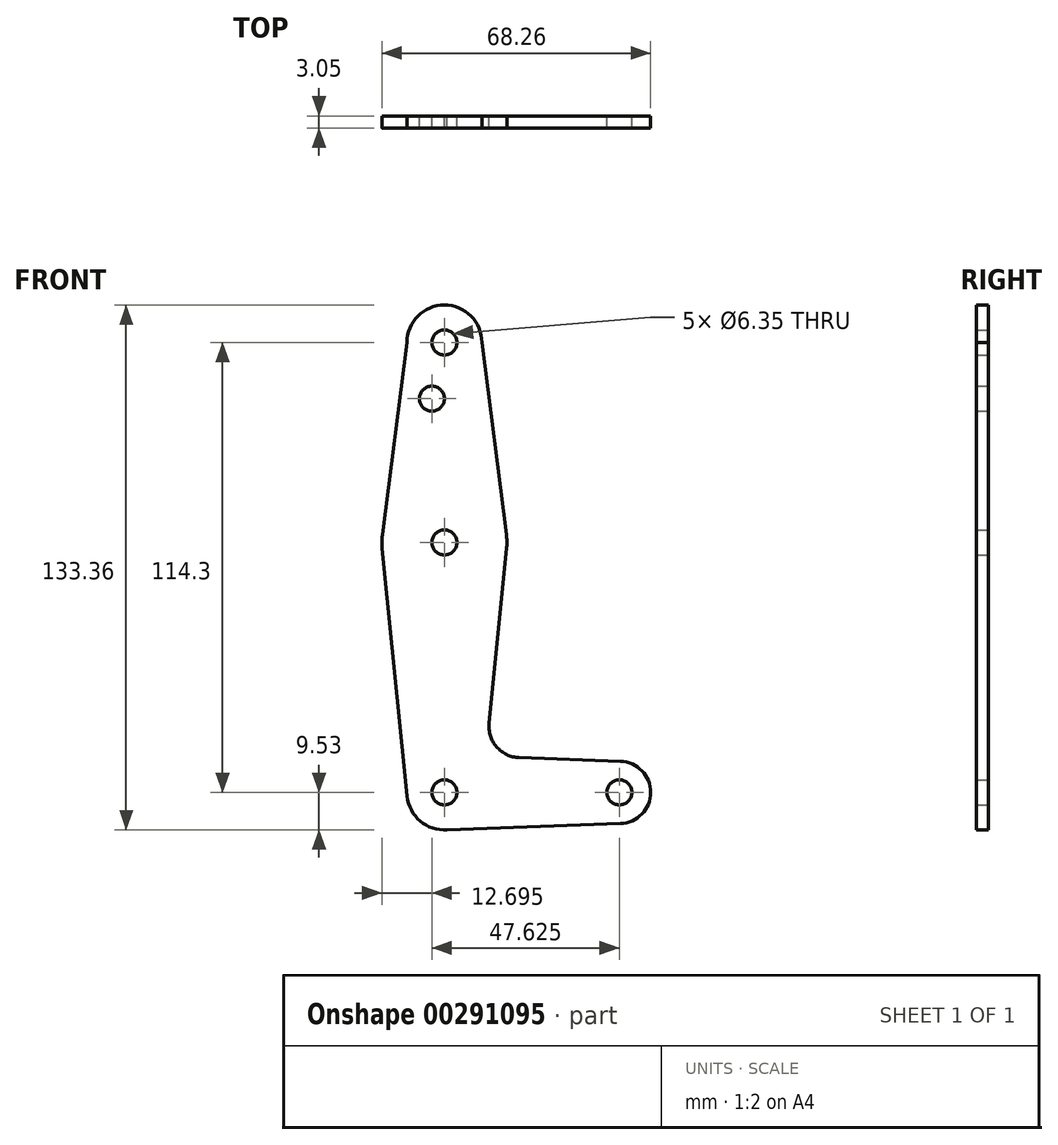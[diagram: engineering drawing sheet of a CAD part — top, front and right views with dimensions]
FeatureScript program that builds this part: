
annotation { "Feature Type Name" : "Feature", "Feature Type Description" : "" }
export const myFeature = defineFeature(function(context is Context, id is Id, definition is map)
    precondition{}
    {
        {
            var Q0;
            Q0=qCreatedBy(makeId("Front.planeOp"),FACE);
            var sketch = newSketch(context, id + "F0", { "sketchPlane" : qUnion([Q0])});
            skLineSegment(sketch, "E0", {"start": v(0, 0) * mm, "end": v(0, 114.3) * mm});
            skLineSegment(sketch, "E1", {"start": v(0, 0) * mm, "end": v(44.45, 0) * mm});
            skCircle(sketch, "E2", {"center": v(0, 114.3) * mm, "radius": 9.53 * mm});
            skCircle(sketch, "E3", {"center": v(0, 63.5) * mm, "radius": 15.88 * mm});
            skCircle(sketch, "E4", {"center": v(0, 0) * mm, "radius": 9.53 * mm});
            skCircle(sketch, "E5", {"center": v(44.45, 0) * mm, "radius": 7.94 * mm});
            skLineSegment(sketch, "E6", {"start": v(-9.53, 114.3) * mm, "end": v(-15.75, 65.5) * mm});
            skLineSegment(sketch, "E7", {"start": v(9.53, 114.3) * mm, "end": v(15.75, 65.5) * mm});
            skLineSegment(sketch, "E8", {"start": v(15.8, 61.91) * mm, "end": v(11.34, 17.59) * mm});
            skLineSegment(sketch, "E9", {"start": v(18.97, 8.85) * mm, "end": v(44.73, 7.93) * mm});
            skLineSegment(sketch, "E10", {"start": v(0, -9.53) * mm, "end": v(44.73, -7.93) * mm});
            skCircle(sketch, "E11", {"center": v(0, 114.3) * mm, "radius": 3.18 * mm});
            skCircle(sketch, "E12", {"center": v(-3.17, 100.03) * mm, "radius": 3.18 * mm});
            skCircle(sketch, "E13", {"center": v(0, 63.5) * mm, "radius": 3.18 * mm});
            skCircle(sketch, "E14", {"center": v(0, 0) * mm, "radius": 3.18 * mm});
            skCircle(sketch, "E15", {"center": v(44.45, 0) * mm, "radius": 3.18 * mm});
            skPoint(sketch, "E16.newPointB", {"position": v(0, 9.53) * mm});
            skArc(sketch, "E16.filletArc", {"start": v(11.34, 17.59) * mm, "mid": v(13.26, 11.57) * mm, "end": v(18.97, 8.85) * mm});
            skLineSegment(sketch, "E17", {"start": v(-15.8, 61.91) * mm, "end": v(-9.48, -0.95) * mm});
            skSolve(sketch);
        }
        {
            var Q0;
            Q0 = qSketchRegion(id + "F0", true);
            var Q1;
            {var subQ0=sQuery(id+"F0.wireOp",EDGE,"E14");var subQ1=sQuery(id+"F0.wireOp",EDGE,"E0");var subQ2=makeQuery(id+"F0.imprint","INTERSECT",VERTEX,{"derivedFrom":[subQ1,subQ0]});Q1=makeQuery(id+"F0.imprint","IMPRINT",FACE,{"disambiguationData":[TD([[makeQuery(id+"F0.imprint","IMPRINT",EDGE,{"disambiguationData":[TD([[subQ2,-1.0]])],"derivedFrom":subQ1}),-1.0]])]});}
            extrude(context, id + "F1", {"entities" : qUnion([Q0, Q1]), "depth" : 3.05 * mm});
        }
    });
